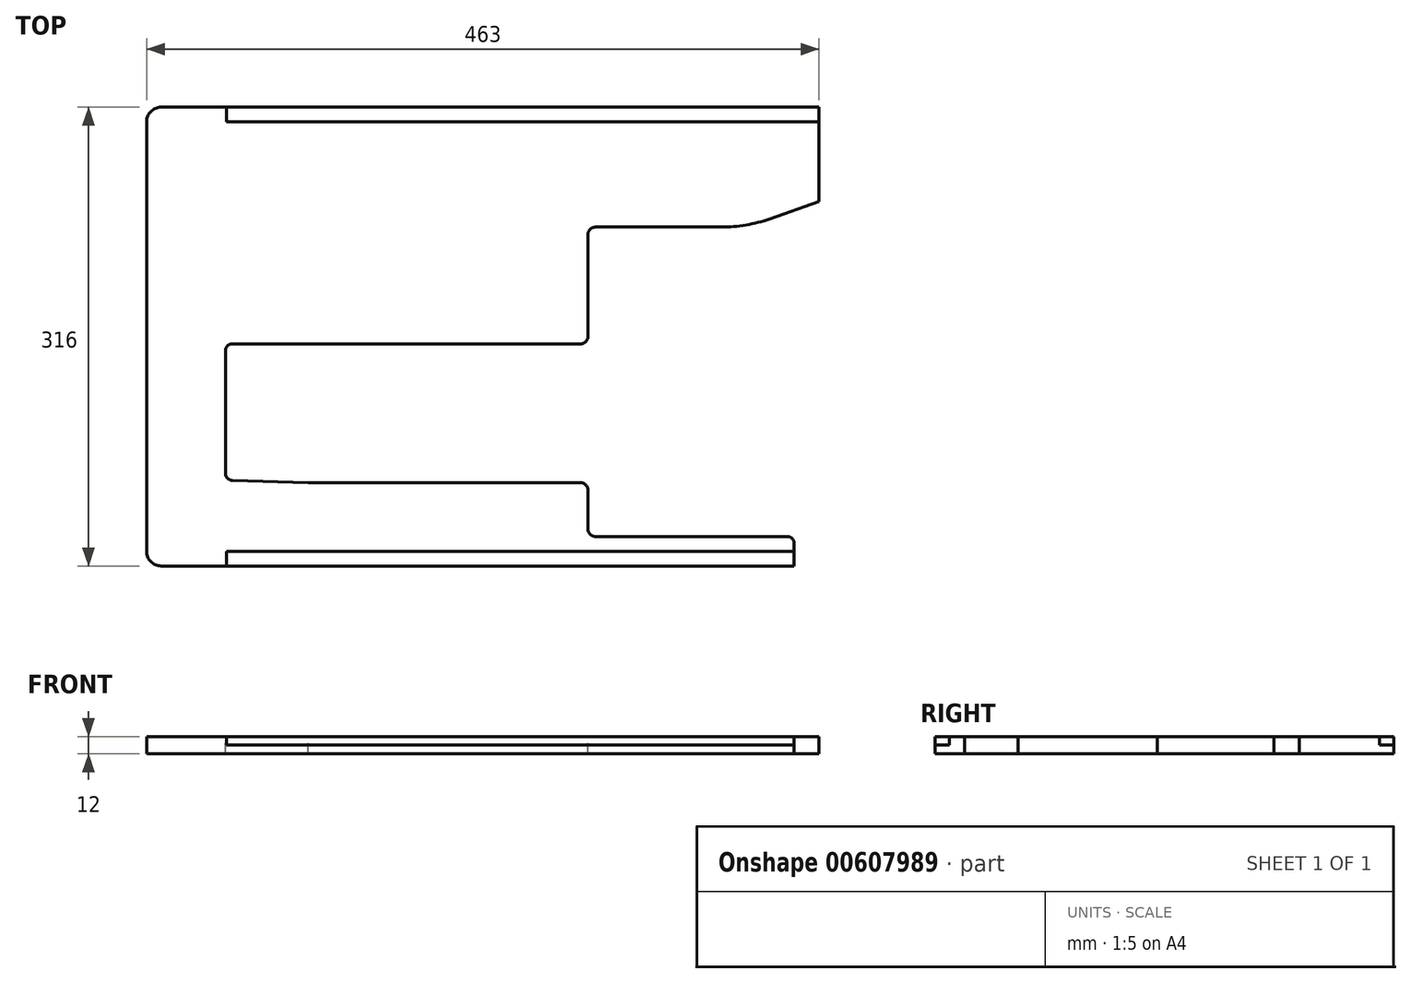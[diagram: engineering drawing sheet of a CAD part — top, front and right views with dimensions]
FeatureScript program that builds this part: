
annotation { "Feature Type Name" : "Feature", "Feature Type Description" : "" }
export const myFeature = defineFeature(function(context is Context, id is Id, definition is map)
    precondition{}
    {
        {
            var Q0;
            Q0=qCreatedBy(makeId("Top.planeOp"),FACE);
            var sketch = newSketch(context, id + "F0", { "sketchPlane" : qUnion([Q0])});
            skLineSegment(sketch, "E0.bottom", {"start": v(0, 0) * mm, "end": v(463, 0) * mm});
            skLineSegment(sketch, "E0.top", {"start": v(0, 316) * mm, "end": v(463, 316) * mm});
            skLineSegment(sketch, "E0.left", {"start": v(0, 0) * mm, "end": v(0, 316) * mm});
            skLineSegment(sketch, "E0.right", {"start": v(463, 0) * mm, "end": v(463, 316) * mm});
            skSolve(sketch);
        }
        {
            var Q0;
            Q0 = qSketchRegion(id + "F0", true);
            extrude(context, id + "F1", {"entities" : qUnion([Q0]), "depth" : 12 * mm, "offsetDistance" : 25 * mm});
        }
        {
            var Q0;
            Q0=makeQuery(id+"F1.opExtrude","CAP_FACE",FACE,{"disambiguationData":[OSD([sQuery(id+"F0.wireOp",EDGE,"E0.bottom"),sQuery(id+"F0.wireOp",EDGE,"E0.top"),sQuery(id+"F0.wireOp",EDGE,"E0.left"),sQuery(id+"F0.wireOp",EDGE,"E0.right")])],"isStart":false});
            var sketch = newSketch(context, id + "F2", { "sketchPlane" : qUnion([Q0])});
            skLineSegment(sketch, "E1.bottom", {"start": v(309, 233.4) * mm, "end": v(395.92, 233.4) * mm});
            skLineSegment(sketch, "E1.top", {"start": v(309, 20.3) * mm, "end": v(446, 20.3) * mm});
            skLineSegment(sketch, "E1.left", {"start": v(304, 228.4) * mm, "end": v(304, 158) * mm});
            skLineSegment(sketch, "E1.right", {"start": v(463, 233.4) * mm, "end": v(463, 20.3) * mm});
            skLineSegment(sketch, "E2.bottom", {"start": v(299, 153) * mm, "end": v(59.3, 153) * mm});
            skLineSegment(sketch, "E2.top", {"start": v(299, 57.3) * mm, "end": v(111.27, 57.3) * mm});
            skLineSegment(sketch, "E2.right", {"start": v(54.3, 148) * mm, "end": v(54.3, 63.85) * mm});
            skLineSegment(sketch, "E3.trimOffspring", {"start": v(304, 52.3) * mm, "end": v(304, 25.3) * mm});
            skPoint(sketch, "E4.visualSharp", {"position": v(54.3, 153) * mm});
            skArc(sketch, "E4.filletArc", {"start": v(59.3, 153) * mm, "mid": v(55.76, 151.54) * mm, "end": v(54.3, 148) * mm});
            skLineSegment(sketch, "E5", {"start": v(59.15, 58.86) * mm, "end": v(111.27, 57.3) * mm});
            skPoint(sketch, "E6.visualSharp", {"position": v(54.3, 59) * mm});
            skArc(sketch, "E6.filletArc", {"start": v(54.3, 63.85) * mm, "mid": v(55.71, 60.37) * mm, "end": v(59.15, 58.86) * mm});
            skPoint(sketch, "E7.visualSharp", {"position": v(304, 153) * mm});
            skArc(sketch, "E7.filletArc", {"start": v(299, 153) * mm, "mid": v(302.54, 154.46) * mm, "end": v(304, 158) * mm});
            skPoint(sketch, "E8.visualSharp", {"position": v(304, 57.3) * mm});
            skArc(sketch, "E8.filletArc", {"start": v(304, 52.3) * mm, "mid": v(302.54, 55.84) * mm, "end": v(299, 57.3) * mm});
            skPoint(sketch, "E9.visualSharp", {"position": v(304, 233.4) * mm});
            skArc(sketch, "E9.filletArc", {"start": v(309, 233.4) * mm, "mid": v(305.46, 231.94) * mm, "end": v(304, 228.4) * mm});
            skPoint(sketch, "E10.visualSharp", {"position": v(304, 20.3) * mm});
            skArc(sketch, "E10.filletArc", {"start": v(304, 25.3) * mm, "mid": v(305.46, 21.76) * mm, "end": v(309, 20.3) * mm});
            skLineSegment(sketch, "E11", {"start": v(429.13, 239.07) * mm, "end": v(463, 251) * mm});
            skLineSegment(sketch, "E12", {"start": v(463, 251) * mm, "end": v(463, 233.4) * mm});
            skPoint(sketch, "E13.visualSharp", {"position": v(413, 233.4) * mm});
            skArc(sketch, "E13.filletArc", {"start": v(395.92, 233.4) * mm, "mid": v(412.76, 234.83) * mm, "end": v(429.13, 239.07) * mm});
            skLineSegment(sketch, "E14.top", {"start": v(446, 0) * mm, "end": v(463, 0) * mm});
            skLineSegment(sketch, "E14.left", {"start": v(446, 20.3) * mm, "end": v(446, 0) * mm});
            skLineSegment(sketch, "E14.right", {"start": v(463, 20.3) * mm, "end": v(463, 0) * mm});
            skSolve(sketch);
        }
        {
            var Q0;
            Q0 = qSketchRegion(id + "F2", true);
            extrude(context, id + "F3", {"entities" : qUnion([Q0]), "operationType" : NewBodyOperationType.REMOVE, "endBound" : BoundingType.THROUGH_ALL, "oppositeDirection" : true, "depth" : 25 * mm, "offsetDistance" : 25 * mm});
        }
        {
            var Q0;
            Q0=makeQuery(id+"F1.opExtrude","CAP_FACE",FACE,{"disambiguationData":[OSD([sQuery(id+"F0.wireOp",EDGE,"E0.bottom"),sQuery(id+"F0.wireOp",EDGE,"E0.top"),sQuery(id+"F0.wireOp",EDGE,"E0.left"),sQuery(id+"F0.wireOp",EDGE,"E0.right")])],"isStart":false});
            var sketch = newSketch(context, id + "F4", { "sketchPlane" : qUnion([Q0])});
            skLineSegment(sketch, "E15.bottom", {"start": v(55, 316) * mm, "end": v(463, 316) * mm});
            skLineSegment(sketch, "E15.top", {"start": v(55, 306) * mm, "end": v(463, 306) * mm});
            skLineSegment(sketch, "E15.left", {"start": v(55, 316) * mm, "end": v(55, 306) * mm});
            skLineSegment(sketch, "E15.right", {"start": v(463, 316) * mm, "end": v(463, 306) * mm});
            skLineSegment(sketch, "E16.bottom", {"start": v(55, 10) * mm, "end": v(446, 10) * mm});
            skLineSegment(sketch, "E16.top", {"start": v(55, 0) * mm, "end": v(446, 0) * mm});
            skLineSegment(sketch, "E16.left", {"start": v(55, 10) * mm, "end": v(55, 0) * mm});
            skLineSegment(sketch, "E16.right", {"start": v(446, 10) * mm, "end": v(446, 0) * mm});
            skSolve(sketch);
        }
        {
            var Q0;
            Q0 = qSketchRegion(id + "F4", true);
            extrude(context, id + "F5", {"entities" : qUnion([Q0]), "operationType" : NewBodyOperationType.REMOVE, "oppositeDirection" : true, "depth" : 5.75 * mm, "offsetDistance" : 25 * mm});
        }
        {
            var Q0;
            Q0=makeQuery(id+"F1.opExtrude","SWEPT_EDGE",EDGE,{"disambiguationData":[OSD([sQuery(id+"F0.wireOp",EDGE,"E0.top"),sQuery(id+"F0.wireOp",EDGE,"E0.left")])]});
            var Q1;
            Q1=makeQuery(id+"F1.opExtrude","SWEPT_EDGE",EDGE,{"disambiguationData":[OSD([sQuery(id+"F0.wireOp",EDGE,"E0.bottom"),sQuery(id+"F0.wireOp",EDGE,"E0.left")])]});
            var Q2;
            Q2=makeQuery(id+"F3.boolean.opBoolean","COPY",EDGE,{"derivedFrom":makeQuery(id+"F3.opExtrude","SWEPT_EDGE",EDGE,{"disambiguationData":[OSD([sQuery(id+"F0.wireOp",EDGE,"E0.right"),sQuery(id+"F2.wireOp",EDGE,"E11"),sQuery(id+"F2.wireOp",EDGE,"E12")])]})});
            fillet(context, id + "F6", {"entities" : qUnion([Q0, Q1, Q2]), "radius" : 10 * mm, "tangentPropagation" : true, "allowEdgeOverflow" : false});
        }
        {
            var Q0;
            Q0=makeQuery(id+"F3.boolean.opBoolean","COPY",EDGE,{"derivedFrom":makeQuery(id+"F3.opExtrude","SWEPT_EDGE",EDGE,{"disambiguationData":[OSD([sQuery(id+"F2.wireOp",EDGE,"E1.top"),sQuery(id+"F2.wireOp",EDGE,"E14.left")])]})});
            fillet(context, id + "F7", {"entities" : qUnion([Q0]), "radius" : 5 * mm, "tangentPropagation" : true, "allowEdgeOverflow" : false});
        }
    });
